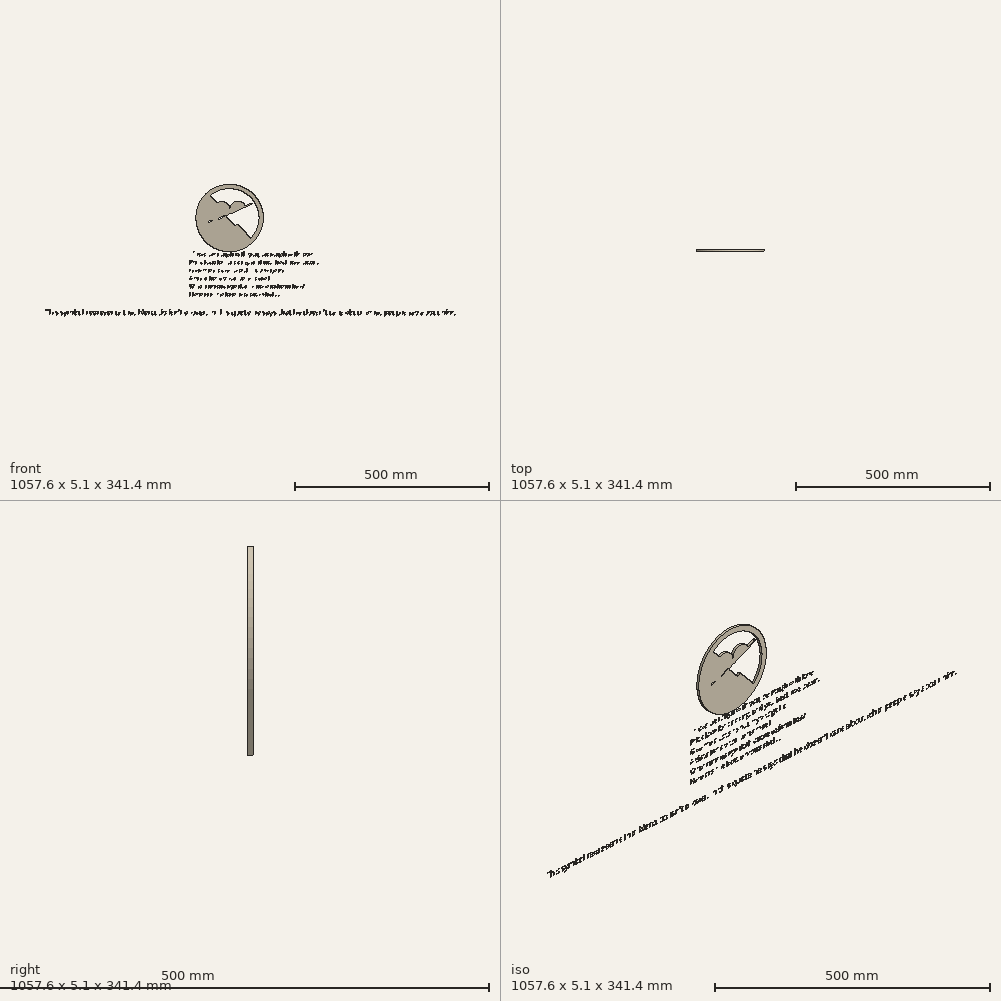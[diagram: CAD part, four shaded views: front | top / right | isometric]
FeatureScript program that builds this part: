
annotation { "Feature Type Name" : "Feature", "Feature Type Description" : "" }
export const myFeature = defineFeature(function(context is Context, id is Id, definition is map)
    precondition{}
    {
        {
            var Q0;
            Q0=qCreatedBy(makeId("Front.planeOp"),FACE);
            var sketch = newSketch(context, id + "F0", { "sketchPlane" : qUnion([Q0])});
            skCircle(sketch, "E0", {"center": v(14, 27.76) * mm, "radius": 20.8 * mm});
            skCircle(sketch, "E1", {"center": v(55.62, 28.47) * mm, "radius": 20.8 * mm});
            skLineSegment(sketch, "E2", {"start": v(-3.89, 17.14) * mm, "end": v(33.2, -35.38) * mm});
            skLineSegment(sketch, "E3", {"start": v(73.07, 17.14) * mm, "end": v(33.2, -35.38) * mm});
            skLineSegment(sketch, "E4", {"start": v(-19.42, -6.28) * mm, "end": v(90.15, 44.48) * mm});
            skLineSegment(sketch, "E5", {"start": v(-19.42, -6.28) * mm, "end": v(-18.03, -9.29) * mm});
            skLineSegment(sketch, "E6", {"start": v(-18.03, -9.29) * mm, "end": v(91.54, 41.47) * mm});
            skLineSegment(sketch, "E7", {"start": v(90.15, 44.48) * mm, "end": v(93.58, 44.48) * mm});
            skLineSegment(sketch, "E8", {"start": v(93.58, 44.48) * mm, "end": v(91.54, 41.47) * mm});
            skLineSegment(sketch, "E9", {"start": v(-18.73, -7.79) * mm, "end": v(93.58, 44.48) * mm});
            skLineSegment(sketch, "E10", {"start": v(-19.42, -6.28) * mm, "end": v(-22.84, -6.28) * mm});
            skLineSegment(sketch, "E11", {"start": v(-22.84, -6.28) * mm, "end": v(-22.84, -4.94) * mm});
            skLineSegment(sketch, "E12", {"start": v(-22.84, -4.94) * mm, "end": v(-16.52, -4.94) * mm});
            skLineSegment(sketch, "E13", {"start": v(-16.52, -4.94) * mm, "end": v(-21.95, -4.94) * mm});
            skLineSegment(sketch, "E14", {"start": v(-21.95, -4.94) * mm, "end": v(-21.95, -3.6) * mm});
            skLineSegment(sketch, "E15", {"start": v(-21.95, -3.6) * mm, "end": v(-13.61, -3.6) * mm});
            skLineSegment(sketch, "E16", {"start": v(-13.61, -3.6) * mm, "end": v(-20.4, -3.6) * mm});
            skLineSegment(sketch, "E17", {"start": v(-20.4, -3.6) * mm, "end": v(-20.4, -2.24) * mm});
            skLineSegment(sketch, "E18", {"start": v(-20.4, -2.24) * mm, "end": v(-10.7, -2.24) * mm});
            skLineSegment(sketch, "E19", {"start": v(-10.7, -2.24) * mm, "end": v(-19, -2.24) * mm});
            skLineSegment(sketch, "E20", {"start": v(-19, -2.24) * mm, "end": v(-19, -0.9) * mm});
            skLineSegment(sketch, "E21", {"start": v(-19, -0.9) * mm, "end": v(-7.8, -0.9) * mm});
            skLineSegment(sketch, "E22.MirrorCS", {"start": v(-13.63, -12.43) * mm, "end": v(-6.42, -3.86) * mm});
            skLineSegment(sketch, "E23.MirrorCS", {"start": v(-15.56, -12.63) * mm, "end": v(-9.32, -5.22) * mm});
            skLineSegment(sketch, "E24.MirrorCS", {"start": v(-12.22, -6.57) * mm, "end": v(-16.6, -11.76) * mm});
            skLineSegment(sketch, "E25.MirrorCS", {"start": v(-19.2, -12.77) * mm, "end": v(-15.12, -7.93) * mm});
            skLineSegment(sketch, "E26.MirrorCS", {"start": v(-18.02, -9.29) * mm, "end": v(-20.22, -11.9) * mm});
            skLineSegment(sketch, "E27.MirrorCS", {"start": v(-20.22, -11.9) * mm, "end": v(-19.2, -12.77) * mm});
            skLineSegment(sketch, "E28.MirrorCS", {"start": v(-18.62, -12.09) * mm, "end": v(-17.6, -12.96) * mm});
            skLineSegment(sketch, "E29.MirrorCS", {"start": v(-16.6, -11.76) * mm, "end": v(-15.56, -12.63) * mm});
            skLineSegment(sketch, "E30.MirrorCS", {"start": v(-14.66, -11.56) * mm, "end": v(-13.63, -12.43) * mm});
            skLineSegment(sketch, "E31", {"start": v(-17.6, -12.96) * mm, "end": v(-16.6, -11.76) * mm});
            skCircle(sketch, "E32", {"center": v(33.8, 5.8) * mm, "radius": 75.9 * mm});
            skCircle(sketch, "E33", {"center": v(33.8, 5.8) * mm, "radius": 87.14 * mm});
            skLineSegment(sketch, "E34", {"start": v(-20.26, 59.06) * mm, "end": v(82.68, -52.25) * mm});
            skLineSegment(sketch, "E35", {"start": v(-15.32, 63.65) * mm, "end": v(88.96, -46.33) * mm});
            skSolve(sketch);
        }
        {
            var Q0;
            Q0=makeQuery(id+"F0.imprint","IMPRINT",FACE,{"disambiguationData":[TD([[makeQuery(id+"F0.imprint","IMPRINT",EDGE,{"derivedFrom":sQuery(id+"F0.wireOp",EDGE,"E33")}),1.0]])]});
            var Q1;
            {var subQ0=sQuery(id+"F0.wireOp",EDGE,"E35");var subQ1=sQuery(id+"F0.wireOp",EDGE,"E0");var subQ2=makeQuery(id+"F0.imprint","INTERSECT",VERTEX,{"disambiguationData":[OD(0.0)],"derivedFrom":[subQ1,subQ0]});Q1=makeQuery(id+"F0.imprint","IMPRINT",FACE,{"disambiguationData":[TD([[makeQuery(id+"F0.imprint","IMPRINT",EDGE,{"disambiguationData":[TD([[subQ2,-1.0]])],"derivedFrom":subQ1}),-1.0]])]});}
            var Q2;
            {var subQ0=sQuery(id+"F0.wireOp",EDGE,"E35");var subQ1=sQuery(id+"F0.wireOp",EDGE,"E0");var subQ2=makeQuery(id+"F0.imprint","INTERSECT",VERTEX,{"disambiguationData":[OD(0.0)],"derivedFrom":[subQ1,subQ0]});Q2=makeQuery(id+"F0.imprint","IMPRINT",FACE,{"disambiguationData":[TD([[makeQuery(id+"F0.imprint","IMPRINT",EDGE,{"disambiguationData":[TD([[subQ2,-1.0]])],"derivedFrom":subQ1}),1.0]])]});}
            var Q3;
            {var subQ0=sQuery(id+"F0.wireOp",EDGE,"E35");var subQ1=sQuery(id+"F0.wireOp",EDGE,"E0");var subQ2=makeQuery(id+"F0.imprint","INTERSECT",VERTEX,{"disambiguationData":[OD(0.0)],"derivedFrom":[subQ1,subQ0]});Q3=makeQuery(id+"F0.imprint","IMPRINT",FACE,{"disambiguationData":[TD([[makeQuery(id+"F0.imprint","IMPRINT",EDGE,{"disambiguationData":[TD([[subQ2,1.0]])],"derivedFrom":subQ1}),1.0]])]});}
            var Q4;
            {var subQ0=sQuery(id+"F0.wireOp",EDGE,"E1");var subQ1=makeQuery(id+"F0.imprint","INTERSECT",VERTEX,{"derivedFrom":[sQuery(id+"F0.wireOp",EDGE,"E0"),subQ0]});Q4=makeQuery(id+"F0.imprint","IMPRINT",FACE,{"disambiguationData":[TD([[makeQuery(id+"F0.imprint","IMPRINT",EDGE,{"disambiguationData":[TD([[subQ1,1.0]])],"derivedFrom":subQ0}),1.0]])]});}
            var Q5;
            {var subQ0=sQuery(id+"F0.wireOp",EDGE,"E9");var subQ1=sQuery(id+"F0.wireOp",EDGE,"E1");var subQ2=makeQuery(id+"F0.imprint","INTERSECT",VERTEX,{"disambiguationData":[OD(0.0)],"derivedFrom":[subQ1,subQ0]});Q5=makeQuery(id+"F0.imprint","IMPRINT",FACE,{"disambiguationData":[TD([[makeQuery(id+"F0.imprint","IMPRINT",EDGE,{"disambiguationData":[TD([[subQ2,-1.0]])],"derivedFrom":subQ1}),1.0]])]});}
            var Q6;
            {var subQ0=sQuery(id+"F0.wireOp",EDGE,"E9");var subQ1=sQuery(id+"F0.wireOp",EDGE,"E1");var subQ2=makeQuery(id+"F0.imprint","INTERSECT",VERTEX,{"disambiguationData":[OD(0.0)],"derivedFrom":[subQ1,subQ0]});Q6=makeQuery(id+"F0.imprint","IMPRINT",FACE,{"disambiguationData":[TD([[makeQuery(id+"F0.imprint","IMPRINT",EDGE,{"disambiguationData":[TD([[subQ2,1.0]])],"derivedFrom":subQ1}),1.0]])]});}
            var Q7;
            {var subQ5=sQuery(id+"F0.wireOp",EDGE,"E7");Q7=makeQuery(id+"F0.imprint","IMPRINT",FACE,{"disambiguationData":[TD([[makeQuery(id+"F0.imprint","IMPRINT",EDGE,{"derivedFrom":subQ5}),-1.0]])]});}
            var Q8;
            {var subQ5=sQuery(id+"F0.wireOp",EDGE,"E8");Q8=makeQuery(id+"F0.imprint","IMPRINT",FACE,{"disambiguationData":[TD([[makeQuery(id+"F0.imprint","IMPRINT",EDGE,{"derivedFrom":subQ5}),-1.0]])]});}
            var Q9;
            {var subQ3=sQuery(id+"F0.wireOp",EDGE,"E35");var subQ6=sQuery(id+"F0.wireOp",EDGE,"E0");var subQ9=makeQuery(id+"F0.imprint","INTERSECT",VERTEX,{"disambiguationData":[OD(1.0)],"derivedFrom":[subQ6,subQ3]});Q9=makeQuery(id+"F0.imprint","IMPRINT",FACE,{"disambiguationData":[TD([[makeQuery(id+"F0.imprint","IMPRINT",EDGE,{"disambiguationData":[TD([[subQ9,-1.0]])],"derivedFrom":subQ6}),-1.0]])]});}
            var Q10;
            {var subQ0=sQuery(id+"F0.wireOp",EDGE,"E9");var subQ1=sQuery(id+"F0.wireOp",EDGE,"E1");var subQ2=makeQuery(id+"F0.imprint","INTERSECT",VERTEX,{"disambiguationData":[OD(1.0)],"derivedFrom":[subQ1,subQ0]});Q10=makeQuery(id+"F0.imprint","IMPRINT",FACE,{"disambiguationData":[TD([[makeQuery(id+"F0.imprint","IMPRINT",EDGE,{"disambiguationData":[TD([[subQ2,-1.0]])],"derivedFrom":subQ1}),-1.0]])]});}
            var Q11;
            {var subQ0=sQuery(id+"F0.wireOp",EDGE,"E35");var subQ1=sQuery(id+"F0.wireOp",EDGE,"E0");var subQ2=makeQuery(id+"F0.imprint","INTERSECT",VERTEX,{"disambiguationData":[OD(1.0)],"derivedFrom":[subQ1,subQ0]});Q11=makeQuery(id+"F0.imprint","IMPRINT",FACE,{"disambiguationData":[TD([[makeQuery(id+"F0.imprint","IMPRINT",EDGE,{"disambiguationData":[TD([[subQ2,-1.0]])],"derivedFrom":subQ1}),1.0]])]});}
            var Q12;
            {var subQ3=sQuery(id+"F0.wireOp",EDGE,"E9");var subQ5=sQuery(id+"F0.wireOp",EDGE,"E0");var subQ6=makeQuery(id+"F0.imprint","INTERSECT",VERTEX,{"disambiguationData":[OD(1.0)],"derivedFrom":[subQ5,subQ3]});Q12=makeQuery(id+"F0.imprint","IMPRINT",FACE,{"disambiguationData":[TD([[makeQuery(id+"F0.imprint","IMPRINT",EDGE,{"disambiguationData":[TD([[subQ6,-1.0]])],"derivedFrom":subQ5}),1.0]])]});}
            var Q13;
            {var subQ0=sQuery(id+"F0.wireOp",EDGE,"E6");var subQ1=sQuery(id+"F0.wireOp",EDGE,"E0");var subQ2=makeQuery(id+"F0.imprint","INTERSECT",VERTEX,{"disambiguationData":[OD(1.0)],"derivedFrom":[subQ1,subQ0]});Q13=makeQuery(id+"F0.imprint","IMPRINT",FACE,{"disambiguationData":[TD([[makeQuery(id+"F0.imprint","IMPRINT",EDGE,{"disambiguationData":[TD([[subQ2,-1.0]])],"derivedFrom":subQ1}),1.0]])]});}
            var Q14;
            {var subQ0=sQuery(id+"F0.wireOp",EDGE,"E9");var subQ1=sQuery(id+"F0.wireOp",EDGE,"E0");var subQ2=makeQuery(id+"F0.imprint","INTERSECT",VERTEX,{"disambiguationData":[OD(0.0)],"derivedFrom":[subQ1,subQ0]});Q14=makeQuery(id+"F0.imprint","IMPRINT",FACE,{"disambiguationData":[TD([[makeQuery(id+"F0.imprint","IMPRINT",EDGE,{"disambiguationData":[TD([[subQ2,-1.0]])],"derivedFrom":subQ1}),-1.0]])]});}
            var Q15;
            {var subQ0=sQuery(id+"F0.wireOp",EDGE,"E2");var subQ1=sQuery(id+"F0.wireOp",EDGE,"E0");var subQ2=makeQuery(id+"F0.imprint","INTERSECT",VERTEX,{"disambiguationData":[OD(1.0)],"derivedFrom":[subQ1,subQ0]});Q15=makeQuery(id+"F0.imprint","IMPRINT",FACE,{"disambiguationData":[TD([[makeQuery(id+"F0.imprint","IMPRINT",EDGE,{"disambiguationData":[TD([[subQ2,-1.0]])],"derivedFrom":subQ1}),-1.0]])]});}
            var Q16;
            {var subQ0=sQuery(id+"F0.wireOp",EDGE,"E4");var subQ1=sQuery(id+"F0.wireOp",EDGE,"E0");var subQ2=makeQuery(id+"F0.imprint","INTERSECT",VERTEX,{"disambiguationData":[OD(0.0)],"derivedFrom":[subQ1,subQ0]});Q16=makeQuery(id+"F0.imprint","IMPRINT",FACE,{"disambiguationData":[TD([[makeQuery(id+"F0.imprint","IMPRINT",EDGE,{"disambiguationData":[TD([[subQ2,-1.0]])],"derivedFrom":subQ1}),1.0]])]});}
            var Q17;
            {var subQ0=sQuery(id+"F0.wireOp",EDGE,"E9");var subQ1=sQuery(id+"F0.wireOp",EDGE,"E0");var subQ2=makeQuery(id+"F0.imprint","INTERSECT",VERTEX,{"disambiguationData":[OD(0.0)],"derivedFrom":[subQ1,subQ0]});Q17=makeQuery(id+"F0.imprint","IMPRINT",FACE,{"disambiguationData":[TD([[makeQuery(id+"F0.imprint","IMPRINT",EDGE,{"disambiguationData":[TD([[subQ2,-1.0]])],"derivedFrom":subQ1}),1.0]])]});}
            var Q18;
            {var subQ0=sQuery(id+"F0.wireOp",EDGE,"E6");var subQ1=sQuery(id+"F0.wireOp",EDGE,"E0");var subQ2=makeQuery(id+"F0.imprint","INTERSECT",VERTEX,{"disambiguationData":[OD(1.0)],"derivedFrom":[subQ1,subQ0]});Q18=makeQuery(id+"F0.imprint","IMPRINT",FACE,{"disambiguationData":[TD([[makeQuery(id+"F0.imprint","IMPRINT",EDGE,{"disambiguationData":[TD([[subQ2,-1.0]])],"derivedFrom":subQ1}),-1.0]])]});}
            var Q19;
            {var subQ0=sQuery(id+"F0.wireOp",EDGE,"E1");var subQ1=sQuery(id+"F0.wireOp",EDGE,"E0");var subQ2=makeQuery(id+"F0.imprint","INTERSECT",VERTEX,{"derivedFrom":[subQ1,subQ0]});Q19=makeQuery(id+"F0.imprint","IMPRINT",FACE,{"disambiguationData":[TD([[makeQuery(id+"F0.imprint","IMPRINT",EDGE,{"disambiguationData":[TD([[subQ2,1.0]])],"derivedFrom":subQ1}),-1.0]])]});}
            var Q20;
            {var subQ0=sQuery(id+"F0.wireOp",EDGE,"E6");var subQ1=sQuery(id+"F0.wireOp",EDGE,"E1");var subQ2=makeQuery(id+"F0.imprint","INTERSECT",VERTEX,{"disambiguationData":[OD(1.0)],"derivedFrom":[subQ1,subQ0]});Q20=makeQuery(id+"F0.imprint","IMPRINT",FACE,{"disambiguationData":[TD([[makeQuery(id+"F0.imprint","IMPRINT",EDGE,{"disambiguationData":[TD([[subQ2,-1.0]])],"derivedFrom":subQ1}),1.0]])]});}
            var Q21;
            {var subQ0=sQuery(id+"F0.wireOp",EDGE,"E2");var subQ1=sQuery(id+"F0.wireOp",EDGE,"E0");var subQ7=makeQuery(id+"F0.imprint","INTERSECT",VERTEX,{"disambiguationData":[OD(0.0)],"derivedFrom":[subQ1,subQ0]});Q21=makeQuery(id+"F0.imprint","IMPRINT",FACE,{"disambiguationData":[TD([[makeQuery(id+"F0.imprint","IMPRINT",EDGE,{"disambiguationData":[TD([[subQ7,1.0]])],"derivedFrom":subQ1}),1.0]])]});}
            var Q22;
            {var subQ0=sQuery(id+"F0.wireOp",EDGE,"E4");var subQ1=sQuery(id+"F0.wireOp",EDGE,"E0");var subQ2=makeQuery(id+"F0.imprint","INTERSECT",VERTEX,{"disambiguationData":[OD(0.0)],"derivedFrom":[subQ1,subQ0]});Q22=makeQuery(id+"F0.imprint","IMPRINT",FACE,{"disambiguationData":[TD([[makeQuery(id+"F0.imprint","IMPRINT",EDGE,{"disambiguationData":[TD([[subQ2,-1.0]])],"derivedFrom":subQ1}),-1.0]])]});}
            var Q23;
            {var subQ0=sQuery(id+"F0.wireOp",EDGE,"E4");var subQ8=sQuery(id+"F0.wireOp",EDGE,"E2");var subQ9=makeQuery(id+"F0.imprint","INTERSECT",VERTEX,{"derivedFrom":[subQ8,subQ0]});Q23=makeQuery(id+"F0.imprint","IMPRINT",FACE,{"disambiguationData":[TD([[makeQuery(id+"F0.imprint","IMPRINT",EDGE,{"disambiguationData":[TD([[subQ9,-1.0]])],"derivedFrom":subQ8}),-1.0]])]});}
            var Q24;
            {var subQ5=sQuery(id+"F0.wireOp",EDGE,"E9");var subQ7=sQuery(id+"F0.wireOp",EDGE,"E2");var subQ8=makeQuery(id+"F0.imprint","INTERSECT",VERTEX,{"derivedFrom":[subQ7,subQ5]});Q24=makeQuery(id+"F0.imprint","IMPRINT",FACE,{"disambiguationData":[TD([[makeQuery(id+"F0.imprint","IMPRINT",EDGE,{"disambiguationData":[TD([[subQ8,-1.0]])],"derivedFrom":subQ7}),-1.0]])]});}
            var Q25;
            {var subQ0=sQuery(id+"F0.wireOp",EDGE,"E19");Q25=makeQuery(id+"F0.imprint","IMPRINT",FACE,{"disambiguationData":[TD([[makeQuery(id+"F0.imprint","IMPRINT",EDGE,{"derivedFrom":subQ0}),-1.0]])]});}
            var Q26;
            {var subQ0=sQuery(id+"F0.wireOp",EDGE,"E16");Q26=makeQuery(id+"F0.imprint","IMPRINT",FACE,{"disambiguationData":[TD([[makeQuery(id+"F0.imprint","IMPRINT",EDGE,{"derivedFrom":subQ0}),-1.0]])]});}
            var Q27;
            {var subQ0=sQuery(id+"F0.wireOp",EDGE,"E13");Q27=makeQuery(id+"F0.imprint","IMPRINT",FACE,{"disambiguationData":[TD([[makeQuery(id+"F0.imprint","IMPRINT",EDGE,{"derivedFrom":subQ0}),-1.0]])]});}
            var Q28;
            {var subQ0=sQuery(id+"F0.wireOp",EDGE,"E10");Q28=makeQuery(id+"F0.imprint","IMPRINT",FACE,{"disambiguationData":[TD([[makeQuery(id+"F0.imprint","IMPRINT",EDGE,{"derivedFrom":subQ0}),-1.0]])]});}
            var Q29;
            {var subQ5=sQuery(id+"F0.wireOp",EDGE,"E30.MirrorCS");Q29=makeQuery(id+"F0.imprint","IMPRINT",FACE,{"disambiguationData":[TD([[makeQuery(id+"F0.imprint","IMPRINT",EDGE,{"derivedFrom":subQ5}),1.0]])]});}
            var Q30;
            {var subQ4=sQuery(id+"F0.wireOp",EDGE,"E29.MirrorCS");Q30=makeQuery(id+"F0.imprint","IMPRINT",FACE,{"disambiguationData":[TD([[makeQuery(id+"F0.imprint","IMPRINT",EDGE,{"derivedFrom":subQ4}),1.0]])]});}
            var Q31;
            {var subQ4=sQuery(id+"F0.wireOp",EDGE,"E28.MirrorCS");Q31=makeQuery(id+"F0.imprint","IMPRINT",FACE,{"disambiguationData":[TD([[makeQuery(id+"F0.imprint","IMPRINT",EDGE,{"derivedFrom":subQ4}),1.0]])]});}
            var Q32;
            {var subQ1=sQuery(id+"F0.wireOp",EDGE,"E26.MirrorCS");Q32=makeQuery(id+"F0.imprint","IMPRINT",FACE,{"disambiguationData":[TD([[makeQuery(id+"F0.imprint","IMPRINT",EDGE,{"derivedFrom":subQ1}),1.0]])]});}
            var Q33;
            {var subQ5=sQuery(id+"F0.wireOp",EDGE,"E6");var subQ6=sQuery(id+"F0.wireOp",EDGE,"E0");var subQ7=makeQuery(id+"F0.imprint","INTERSECT",VERTEX,{"disambiguationData":[OD(0.0)],"derivedFrom":[subQ6,subQ5]});Q33=makeQuery(id+"F0.imprint","IMPRINT",FACE,{"disambiguationData":[TD([[makeQuery(id+"F0.imprint","IMPRINT",EDGE,{"disambiguationData":[TD([[subQ7,-1.0]])],"derivedFrom":subQ6}),-1.0]])]});}
            var Q34;
            {var subQ0=sQuery(id+"F0.wireOp",EDGE,"E6");var subQ1=sQuery(id+"F0.wireOp",EDGE,"E1");var subQ2=makeQuery(id+"F0.imprint","INTERSECT",VERTEX,{"disambiguationData":[OD(1.0)],"derivedFrom":[subQ1,subQ0]});Q34=makeQuery(id+"F0.imprint","IMPRINT",FACE,{"disambiguationData":[TD([[makeQuery(id+"F0.imprint","IMPRINT",EDGE,{"disambiguationData":[TD([[subQ2,-1.0]])],"derivedFrom":subQ1}),-1.0]])]});}
            var Q35;
            {var subQ0=sQuery(id+"F0.wireOp",EDGE,"E35");var subQ1=sQuery(id+"F0.wireOp",EDGE,"E3");var subQ2=makeQuery(id+"F0.imprint","INTERSECT",VERTEX,{"derivedFrom":[subQ1,subQ0]});Q35=makeQuery(id+"F0.imprint","IMPRINT",FACE,{"disambiguationData":[TD([[makeQuery(id+"F0.imprint","IMPRINT",EDGE,{"disambiguationData":[TD([[subQ2,-1.0]])],"derivedFrom":subQ1}),1.0]])]});}
            var Q36;
            {var subQ0=sQuery(id+"F0.wireOp",EDGE,"E6");var subQ1=sQuery(id+"F0.wireOp",EDGE,"E0");var subQ2=makeQuery(id+"F0.imprint","INTERSECT",VERTEX,{"disambiguationData":[OD(0.0)],"derivedFrom":[subQ1,subQ0]});Q36=makeQuery(id+"F0.imprint","IMPRINT",FACE,{"disambiguationData":[TD([[makeQuery(id+"F0.imprint","IMPRINT",EDGE,{"disambiguationData":[TD([[subQ2,-1.0]])],"derivedFrom":subQ1}),1.0]])]});}
            var Q37;
            {var subQ0=sQuery(id+"F0.wireOp",EDGE,"E34");var subQ1=sQuery(id+"F0.wireOp",EDGE,"E0");var subQ2=makeQuery(id+"F0.imprint","INTERSECT",VERTEX,{"disambiguationData":[OD(1.0)],"derivedFrom":[subQ1,subQ0]});Q37=makeQuery(id+"F0.imprint","IMPRINT",FACE,{"disambiguationData":[TD([[makeQuery(id+"F0.imprint","IMPRINT",EDGE,{"disambiguationData":[TD([[subQ2,-1.0]])],"derivedFrom":subQ1}),1.0]])]});}
            var Q38;
            {var subQ0=sQuery(id+"F0.wireOp",EDGE,"E34");var subQ1=sQuery(id+"F0.wireOp",EDGE,"E0");var subQ2=makeQuery(id+"F0.imprint","INTERSECT",VERTEX,{"disambiguationData":[OD(1.0)],"derivedFrom":[subQ1,subQ0]});Q38=makeQuery(id+"F0.imprint","IMPRINT",FACE,{"disambiguationData":[TD([[makeQuery(id+"F0.imprint","IMPRINT",EDGE,{"disambiguationData":[TD([[subQ2,-1.0]])],"derivedFrom":subQ1}),-1.0]])]});}
            extrude(context, id + "F1", {"entities" : qUnion([Q0, Q1, Q2, Q3, Q4, Q5, Q6, Q7, Q8, Q9, Q10, Q11, Q12, Q13, Q14, Q15, Q16, Q17, Q18, Q19, Q20, Q21, Q22, Q23, Q24, Q25, Q26, Q27, Q28, Q29, Q30, Q31, Q32, Q33, Q34, Q35, Q36, Q37, Q38]), "depth" : 5.08 * mm, "offsetDistance" : 25.4 * mm});
        }
        {
            var Q0;
            Q0=qCreatedBy(makeId("Front.planeOp"),FACE);
            var sketch = newSketch(context, id + "F2", { "sketchPlane" : qUnion([Q0])});
            skText(sketch, "E36", { "text": " If love be rough with you, be rough with love; \nPrick love for pricking, and you beat love down. \nGive me a case to put my visage in: \nA visor for a visor! what care I \nWhat curious eye doth quote deformities? \nHere are the beetle brows shall...", "fontName": "OpenSans-Regular.ttf"});
            const initialGuessF2  = {"E36": [-0.07038, -0.09322, 1, 0, 0.01096]};
            skSetInitialGuess(sketch, initialGuessF2);
            skSolve(sketch);
        }
        {
            var Q0;
            Q0=qCreatedBy(makeId("Front.planeOp"),FACE);
            var sketch = newSketch(context, id + "F3", { "sketchPlane" : qUnion([Q0])});
            skText(sketch, "E37", { "text": "This symbol represents that Mercutio isn\'t a lover. In this quote he says that he doesn\'t care about what people say about him.  ", "fontName": "OpenSans-Regular.ttf"});
            const initialGuessF3  = {"E37": [-0.44134, -0.24414, 1, 0, 0.01298]};
            skSetInitialGuess(sketch, initialGuessF3);
            skSolve(sketch);
        }
        {
            var Q0;
            Q0 = qSketchRegion(id + "F3", true);
            var Q1;
            Q1 = qSketchRegion(id + "F2", true);
            extrude(context, id + "F4", {"entities" : qUnion([Q0, Q1]), "depth" : 0.05 * mm, "offsetDistance" : 25.4 * mm});
        }
    });
